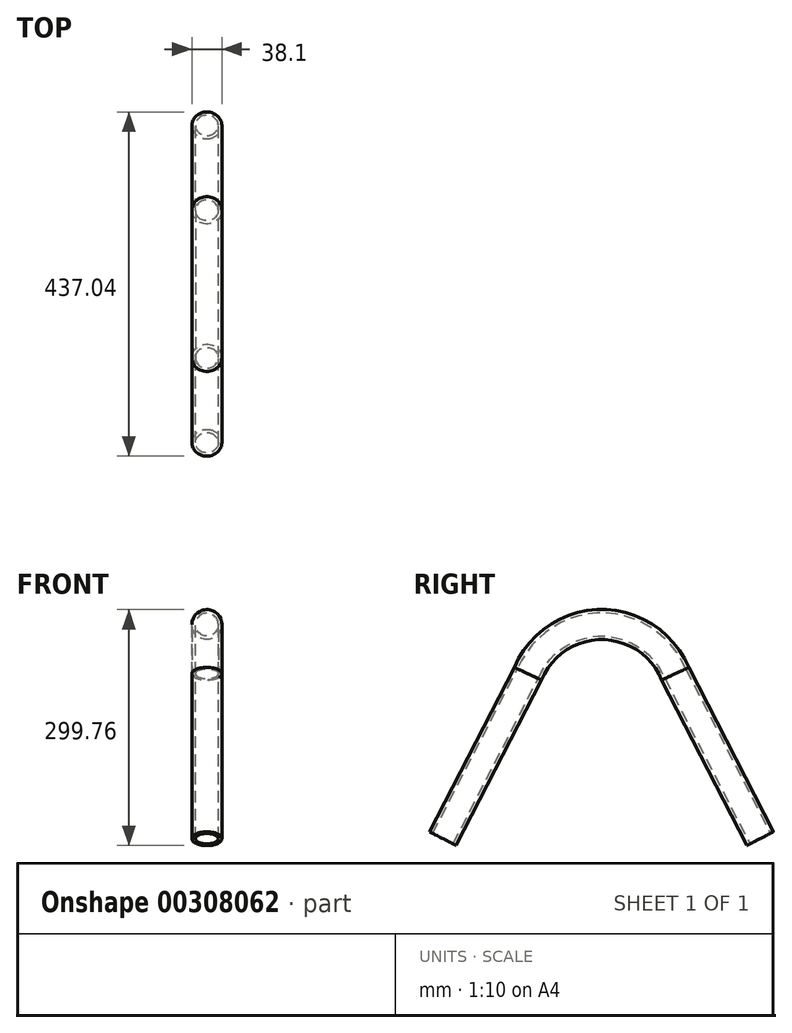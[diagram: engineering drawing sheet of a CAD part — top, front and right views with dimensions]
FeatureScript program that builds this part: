
annotation { "Feature Type Name" : "Feature", "Feature Type Description" : "" }
export const myFeature = defineFeature(function(context is Context, id is Id, definition is map)
    precondition{}
    {
        {
            var Q0;
            Q0=qCreatedBy(makeId("Right.planeOp"),FACE);
            var sketch = newSketch(context, id + "F0", { "sketchPlane" : qUnion([Q0])});
            skPoint(sketch, "E0", {"position": v(-29.58, 193.04) * mm});
            skArc(sketch, "E1", {"start": v(64.2, 232.11) * mm, "mid": v(-29.58, 294.64) * mm, "end": v(-123.36, 232.11) * mm});
            skLineSegment(sketch, "E2", {"start": v(-231.31, 22.56) * mm, "end": v(-123.36, 232.11) * mm});
            skLineSegment(sketch, "E3", {"start": v(172.15, 22.56) * mm, "end": v(64.2, 232.11) * mm});
            skLineSegment(sketch, "E4.0", {"start": v(-248.25, 31.29) * mm, "end": v(-140.3, 240.84) * mm});
            skArc(sketch, "E5.0", {"start": v(81.79, 239.44) * mm, "mid": v(-29.58, 313.69) * mm, "end": v(-140.95, 239.44) * mm});
            skLineSegment(sketch, "E6.0", {"start": v(189.09, 31.29) * mm, "end": v(81.14, 240.84) * mm});
            skLineSegment(sketch, "E7", {"start": v(-231.31, 22.56) * mm, "end": v(-248.25, 31.29) * mm});
            skLineSegment(sketch, "E8", {"start": v(172.15, 22.56) * mm, "end": v(189.09, 31.29) * mm});
            skSolve(sketch);
        }
        {
            var Q0;
            Q0=sQuery(id+"F0.wireOp",EDGE,"E7");
            cPlane(context, id + "F1", {"entities" : qUnion([Q0]), "cplaneType" : CPlaneType.LINE_ANGLE, "offset" : 25.4 * mm, "angle" : 0 * degree, "width" : 152.4 * mm, "height" : 152.4 * mm});
        }
        {
            var Q0;
            Q0=qCreatedBy(id+"F1.planeOp",FACE);
            var sketch = newSketch(context, id + "F2", { "sketchPlane" : qUnion([Q0])});
            skCircle(sketch, "E9", {"center": v(0, 215.8) * mm, "radius": 19.05 * mm});
            skCircle(sketch, "E10", {"center": v(0, 215.8) * mm, "radius": 14.6 * mm});
            skSolve(sketch);
        }
        {
            var Q0;
            Q0=makeQuery(id+"F2.imprint","IMPRINT",FACE,{"disambiguationData":[TD([[makeQuery(id+"F2.imprint","IMPRINT",EDGE,{"derivedFrom":sQuery(id+"F2.wireOp",EDGE,"E9")}),1.0]])]});
            var Q1;
            Q1=sQuery(id+"F0.wireOp",EDGE,"E2");
            var Q2;
            Q2=sQuery(id+"F0.wireOp",EDGE,"E1");
            var Q3;
            Q3=sQuery(id+"F0.wireOp",EDGE,"E3");
            sweep(context, id + "F3", {"profiles" : qUnion([Q0]), "path" : qUnion([Q1, Q2, Q3])});
        }
    });
